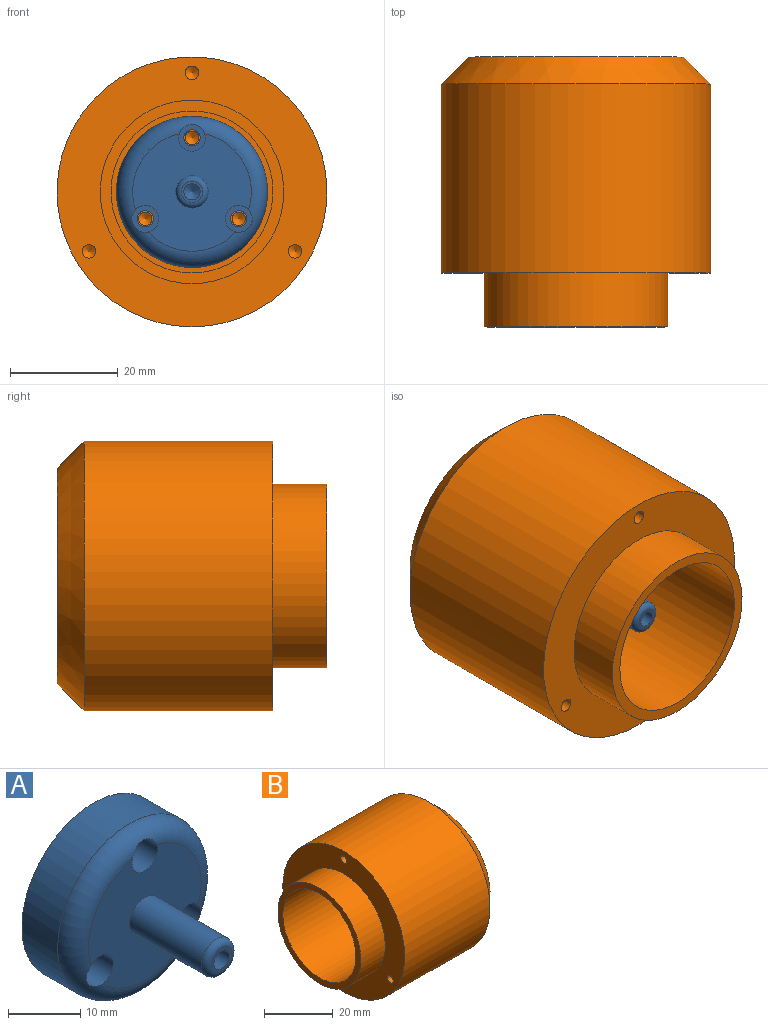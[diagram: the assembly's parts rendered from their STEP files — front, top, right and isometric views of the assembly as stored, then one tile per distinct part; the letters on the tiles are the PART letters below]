
ASSEMBLY  parts=2 mates=1
PART A: 20 faces, bbox 30.3x25x30.3 mm
  f0: plane 22x21.74mm, normal (0,-1,0), area 309mm2, adj f3,f6,f13,f16,f19
  f1: cylinder r=14mm len=28mm, axis (0,1,0), area 615.8mm2, adj f2,f6
  f2: plane 28x28mm, normal (0,1,0), area 574.9mm2, adj f1,f9,f11,f14,f17
  f3: cylinder r=3mm len=14mm, axis (0,1,0), area 263.9mm2, adj f0,f5
  f4: plane 4x4mm, normal (0,-1,0), area 5.5mm2, adj f5,f7
  f5: torus R=2mm, axis (0,-1,0), area 26mm2, adj f3,f4
  f6: torus R=11mm, axis (0,-1,0), area 365.7mm2, adj f0,f1,f13,f16,f19
  f7: cylinder r=1.5mm len=12mm, axis (0,-1,0), area 113.1mm2, adj f4,f8
  f8: cone r=0mm half-angle=59deg, axis (0,-1,0), area 8.2mm2, adj f7
  f9: cylinder r=2.5mm len=10mm, axis (0,1,0), area 157.1mm2, adj f2,f10
  f10: cone r=0mm half-angle=59deg, axis (0,1,0), area 22.9mm2, adj f9
  f11: cylinder r=1.5mm len=5mm, axis (0,-1,0), area 47.1mm2, adj f2,f12
  f12: plane 5x5mm, normal (0,-1,0), area 12.6mm2, adj f11,f13
  f13: cylinder r=2.5mm len=5mm, axis (0,-1,0), area 77.2mm2, adj f0,f6,f12
  f14: cylinder r=1.5mm len=5mm, axis (0,-1,0), area 47.1mm2, adj f2,f15
  f15: plane 5x5mm, normal (0,-1,0), area 12.6mm2, adj f14,f16
  f16: cylinder r=2.5mm len=5mm, axis (0,-1,0), area 77.2mm2, adj f0,f6,f15
  f17: cylinder r=1.5mm len=5mm, axis (0,-1,0), area 47.1mm2, adj f2,f18
  f18: plane 5x5mm, normal (0,-1,0), area 12.6mm2, adj f17,f19
  f19: cylinder r=2.5mm len=5mm, axis (0,-1,0), area 77.2mm2, adj f0,f6,f18
PART B: 21 faces, bbox 50x50x50 mm
  f0: plane 40x40mm, normal (1,0,0), area 1102.7mm2, adj f1,f8
  f1: cone r=25mm half-angle=45deg, axis (-1,0,0), area 999.6mm2, adj f0,f2
  f2: cylinder r=25mm len=50mm, axis (1,0,0), area 5497.8mm2, adj f1,f3
  f3: plane 50x50mm, normal (-1,0,0), area 1040.8mm2, adj f2,f4,f9,f11,f13
  f4: cylinder r=17mm len=34mm, axis (1,0,0), area 1068.1mm2, adj f3,f5
  f5: plane 34x34mm, normal (-1,0,0), area 201.1mm2, adj f4,f6
  f6: cylinder r=15mm len=33mm, axis (1,0,0), area 3110.2mm2, adj f5,f7
  f7: plane 30x30mm, normal (-1,0,0), area 579mm2, adj f6,f8,f15,f17,f19
  f8: cone r=6mm half-angle=3.4deg, axis (1,0,0), area 695.5mm2, adj f0,f7
  f9: cylinder r=1.25mm len=12mm, axis (-1,0,0), area 94.2mm2, adj f3,f10
  f10: cone r=0mm half-angle=59deg, axis (-1,0,0), area 5.7mm2, adj f9
  f11: cylinder r=1.25mm len=12mm, axis (-1,0,0), area 94.2mm2, adj f3,f12
  f12: cone r=0mm half-angle=59deg, axis (-1,0,0), area 5.7mm2, adj f11
  f13: cylinder r=1.25mm len=12mm, axis (-1,0,0), area 94.2mm2, adj f3,f14
  f14: cone r=0mm half-angle=59deg, axis (-1,0,0), area 5.7mm2, adj f13
  f15: cylinder r=1.25mm len=12mm, axis (-1,0,0), area 94.2mm2, adj f7,f16
  f16: cone r=0mm half-angle=59deg, axis (-1,0,0), area 5.7mm2, adj f15
  f17: cylinder r=1.25mm len=12mm, axis (-1,0,0), area 94.2mm2, adj f7,f18
  f18: cone r=0mm half-angle=59deg, axis (-1,0,0), area 5.7mm2, adj f17
  f19: cylinder r=1.25mm len=12mm, axis (-1,0,0), area 94.2mm2, adj f7,f20
  f20: cone r=0mm half-angle=59deg, axis (-1,0,0), area 5.7mm2, adj f19
PLACE A t=(-27.13,-69.48,-7.99)mm
PLACE B rot(axis=(0,0,1),90deg) t=(-27.13,-69.48,-7.99)mm
MATE fastened B.f1 <-> A.f1  axis (0,1,0) through (-27.13,-69.48,-7.99)mm
